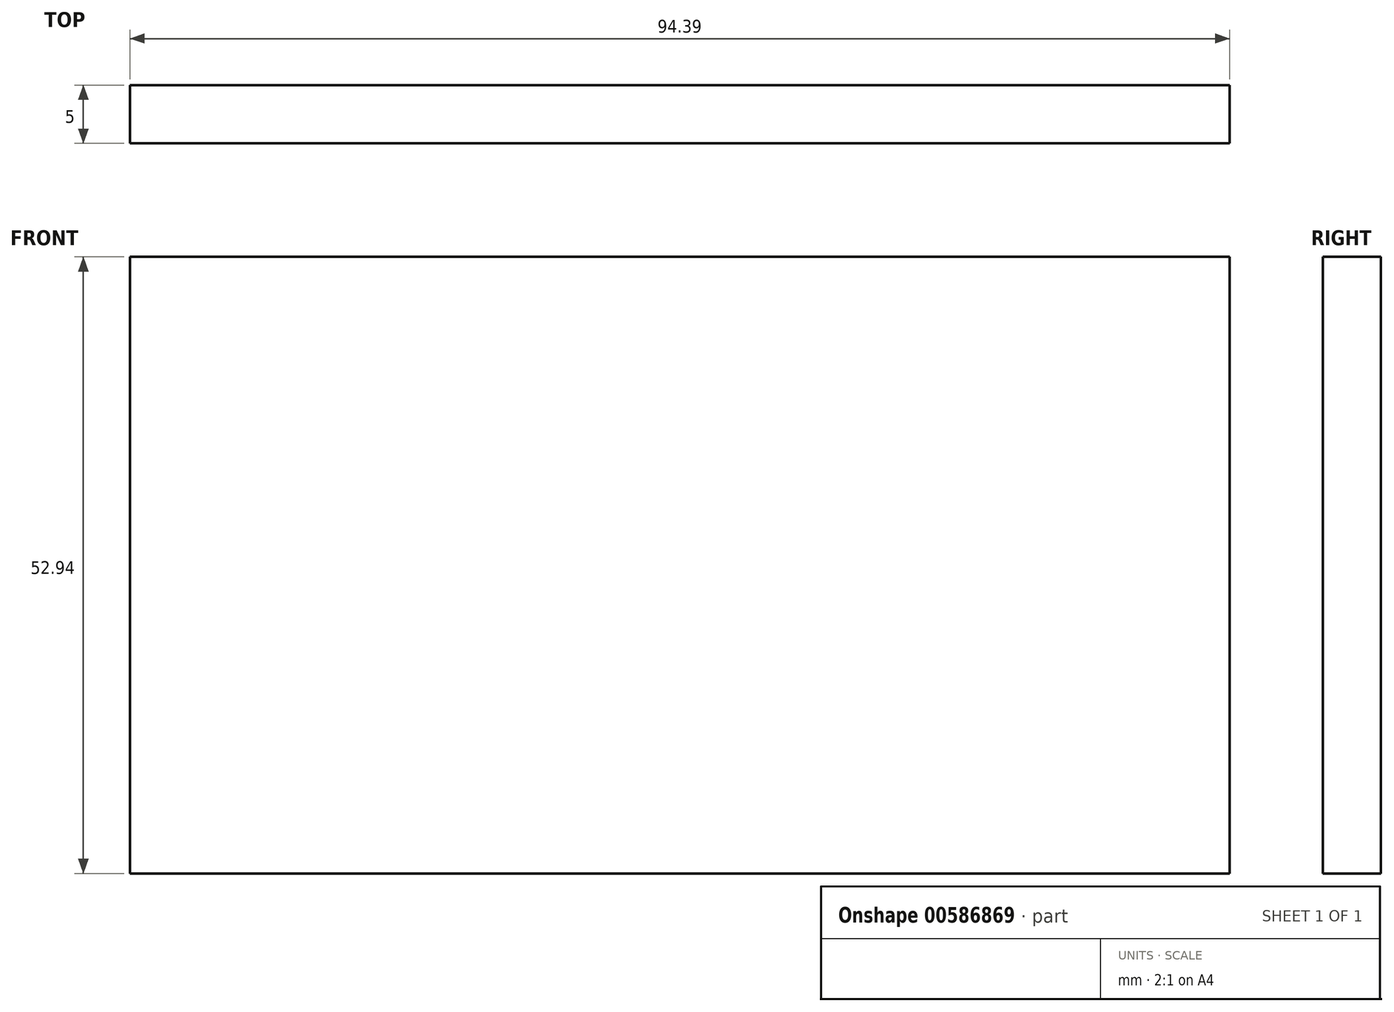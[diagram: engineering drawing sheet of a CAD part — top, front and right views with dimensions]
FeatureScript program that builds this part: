
annotation { "Feature Type Name" : "Feature", "Feature Type Description" : "" }
export const myFeature = defineFeature(function(context is Context, id is Id, definition is map)
    precondition{}
    {
        {
            var Q0;
            Q0=qCreatedBy(makeId("Front.planeOp"),FACE);
            var sketch = newSketch(context, id + "F0", { "sketchPlane" : qUnion([Q0])});
            skLineSegment(sketch, "E0.bottom", {"start": v(-42.67, 21.95) * mm, "end": v(51.72, 21.95) * mm});
            skLineSegment(sketch, "E0.top", {"start": v(-42.67, -31) * mm, "end": v(51.72, -31) * mm});
            skLineSegment(sketch, "E0.left", {"start": v(-42.67, 21.95) * mm, "end": v(-42.67, -31) * mm});
            skLineSegment(sketch, "E0.right", {"start": v(51.72, 21.95) * mm, "end": v(51.72, -31) * mm});
            skSolve(sketch);
        }
        {
            var Q0;
            Q0=makeQuery(id+"F0.imprint","IMPRINT",FACE,{"disambiguationData":[TD([[makeQuery(id+"F0.imprint","IMPRINT",EDGE,{"derivedFrom":sQuery(id+"F0.wireOp",EDGE,"E0.bottom")}),-1.0]])]});
            extrude(context, id + "F1", {"entities" : qUnion([Q0]), "depth" : 5 * mm, "offsetDistance" : 25 * mm});
        }
    });
